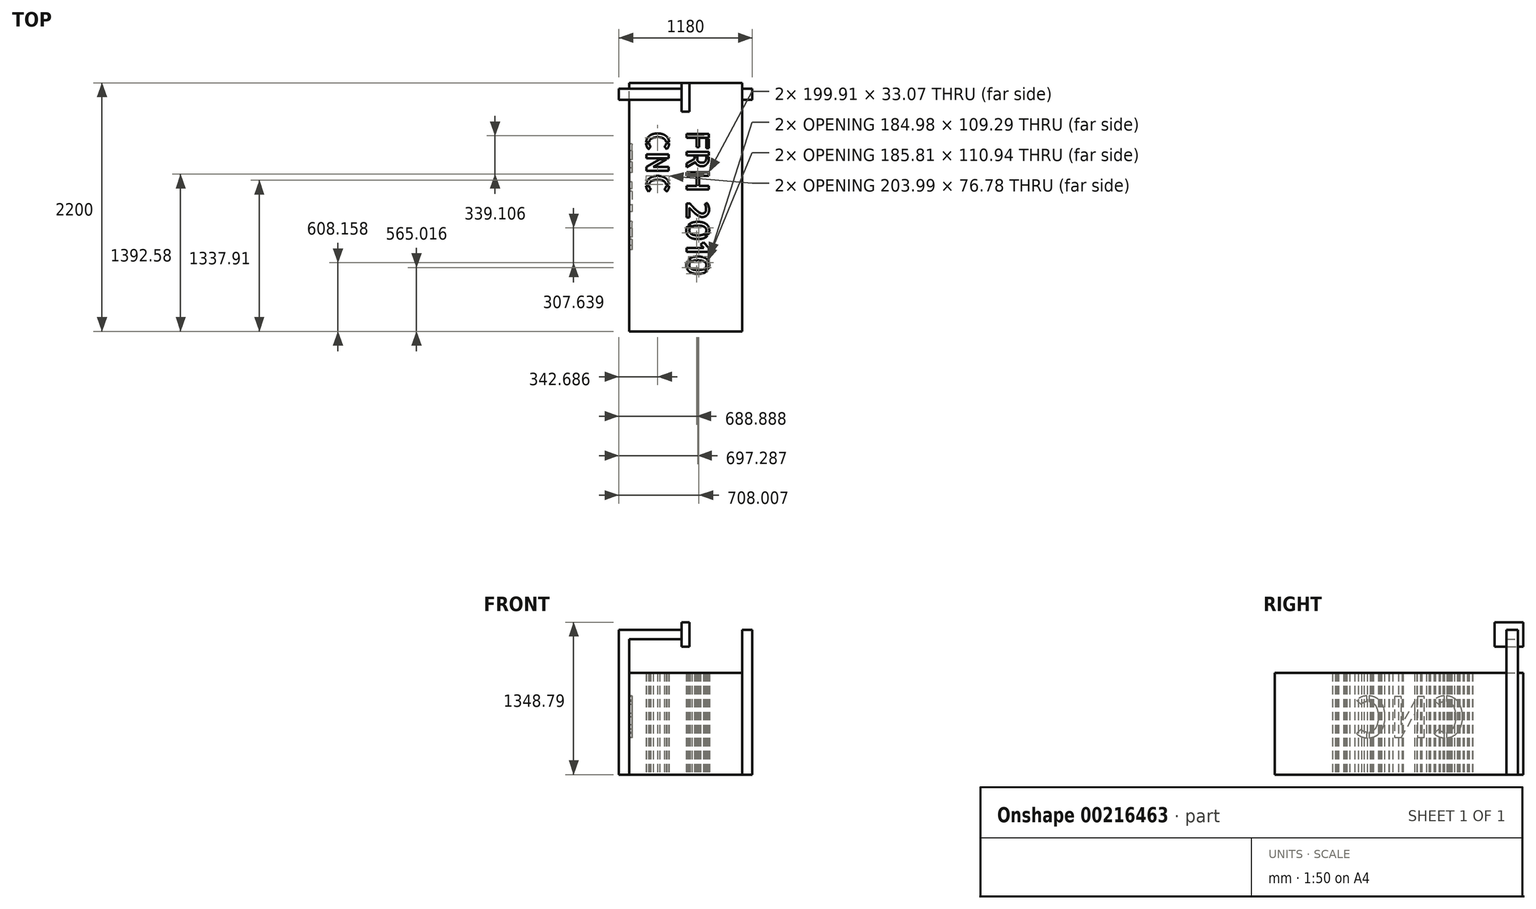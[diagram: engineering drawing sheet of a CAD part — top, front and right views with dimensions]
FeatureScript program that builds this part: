
annotation { "Feature Type Name" : "Feature", "Feature Type Description" : "" }
export const myFeature = defineFeature(function(context is Context, id is Id, definition is map)
    precondition{}
    {
        {
            var Q0;
            Q0=qCreatedBy(makeId("Top.planeOp"),FACE);
            var sketch = newSketch(context, id + "F0", { "sketchPlane" : qUnion([Q0])});
            skLineSegment(sketch, "E0.bottom", {"start": v(1025.88, 14.14) * mm, "end": v(25.88, 14.14) * mm});
            skLineSegment(sketch, "E0.top", {"start": v(1025.88, 2214.14) * mm, "end": v(25.88, 2214.14) * mm});
            skLineSegment(sketch, "E0.left", {"start": v(1025.88, 14.14) * mm, "end": v(1025.88, 2214.14) * mm});
            skLineSegment(sketch, "E0.right", {"start": v(25.88, 14.14) * mm, "end": v(25.88, 2214.14) * mm});
            skText(sketch, "E1", { "text": "FRH 2010\nCNC", "fontName": "AllertaStencil-Regular.ttf"});
            const initialGuessF0  = {"E1": [0.53321, 1.78814, 0, -1, 0.2]};
            skSetInitialGuess(sketch, initialGuessF0);
            skSolve(sketch);
        }
        {
            var Q0;
            Q0=makeQuery(id+"F0.imprint","IMPRINT",FACE,{"disambiguationData":[TD([[makeQuery(id+"F0.imprint","IMPRINT",EDGE,{"derivedFrom":sQuery(id+"F0.wireOp",EDGE,"E0.bottom")}),-1.0]])]});
            extrude(context, id + "F1", {"entities" : qUnion([Q0]), "depth" : 900 * mm});
        }
        {
            var Q0;
            Q0=makeQuery(id+"F1.opExtrude","SWEPT_FACE",FACE,{"disambiguationData":[OSD([sQuery(id+"F0.wireOp",EDGE,"E0.top")])]});
            var sketch = newSketch(context, id + "F2", { "sketchPlane" : qUnion([Q0])});
            skLineSegment(sketch, "E2.bottom", {"start": v(-1025.88, 0) * mm, "end": v(-1115.88, 0) * mm});
            skLineSegment(sketch, "E2.top", {"start": v(-1025.88, 1280) * mm, "end": v(-1115.88, 1280) * mm});
            skLineSegment(sketch, "E2.left", {"start": v(-1025.88, 0) * mm, "end": v(-1025.88, 1280) * mm});
            skLineSegment(sketch, "E2.right", {"start": v(-1115.88, 0) * mm, "end": v(-1115.88, 1280) * mm});
            skLineSegment(sketch, "E3.bottom", {"start": v(-1025.88, 1280) * mm, "end": v(-25.88, 1280) * mm});
            skLineSegment(sketch, "E3.top", {"start": v(-1025.88, 1200) * mm, "end": v(-25.88, 1200) * mm});
            skLineSegment(sketch, "E3.left", {"start": v(-1025.88, 1280) * mm, "end": v(-1025.88, 1200) * mm});
            skLineSegment(sketch, "E3.right", {"start": v(-25.88, 1280) * mm, "end": v(-25.88, 1200) * mm});
            skLineSegment(sketch, "E4", {"start": v(-525.88, -229.17) * mm, "end": v(-525.88, -541.3) * mm, "construction": true});
            skPoint(sketch, "E4.startSnap0", {"position": v(-525.88, 0) * mm});
            skLineSegment(sketch, "E5.MirrorCS", {"start": v(-25.88, 0) * mm, "end": v(-25.88, 1280) * mm});
            skLineSegment(sketch, "E6.MirrorCS", {"start": v(64.12, 0) * mm, "end": v(64.12, 1280) * mm});
            skLineSegment(sketch, "E7.MirrorCS", {"start": v(-25.88, 0) * mm, "end": v(64.12, 0) * mm});
            skLineSegment(sketch, "E8.MirrorCS", {"start": v(-25.88, 1280) * mm, "end": v(64.12, 1280) * mm});
            skPoint(sketch, "E9", {"position": v(-525.88, 1200) * mm});
            skLineSegment(sketch, "E10.bottom", {"start": v(-490.88, 1348.8) * mm, "end": v(-560.88, 1348.8) * mm});
            skLineSegment(sketch, "E10.top", {"start": v(-490.88, 1131.2) * mm, "end": v(-560.88, 1131.2) * mm});
            skLineSegment(sketch, "E10.left", {"start": v(-490.88, 1348.8) * mm, "end": v(-490.88, 1131.2) * mm});
            skLineSegment(sketch, "E10.right", {"start": v(-560.88, 1348.8) * mm, "end": v(-560.88, 1131.2) * mm});
            skPoint(sketch, "E10.middle", {"position": v(-525.88, 1240) * mm});
            skPoint(sketch, "E10.middle.positionSnap0", {"position": v(-1025.88, 1240) * mm});
            skPoint(sketch, "E10.centerSnap0", {"position": v(-1025.88, 1240) * mm});
            skSolve(sketch);
        }
        {
            var Q0;
            {var subQ0=sQuery(id+"F2.wireOp",EDGE,"E5.MirrorCS");var subQ5=sQuery(id+"F2.wireOp",EDGE,"E3.top");var subQ6=makeQuery(id+"F2.imprint","INTERSECT",VERTEX,{"derivedFrom":[subQ5,subQ0]});Q0=makeQuery(id+"F2.imprint","IMPRINT",FACE,{"disambiguationData":[TD([[makeQuery(id+"F2.imprint","IMPRINT",EDGE,{"disambiguationData":[TD([[subQ6,1.0]])],"derivedFrom":subQ5}),1.0]])]});}
            var Q1;
            {var subQ0=sQuery(id+"F2.wireOp",EDGE,"E3.left");Q1=makeQuery(id+"F2.imprint","IMPRINT",FACE,{"disambiguationData":[TD([[makeQuery(id+"F2.imprint","IMPRINT",EDGE,{"derivedFrom":subQ0}),1.0]])]});}
            var Q2;
            {var subQ4=sQuery(id+"F2.wireOp",EDGE,"E2.bottom");Q2=makeQuery(id+"F2.imprint","IMPRINT",FACE,{"disambiguationData":[TD([[makeQuery(id+"F2.imprint","IMPRINT",EDGE,{"derivedFrom":subQ4}),-1.0]])]});}
            var Q3;
            Q3=makeQuery(id+"F2.imprint","IMPRINT",FACE,{"disambiguationData":[TD([[makeQuery(id+"F2.imprint","IMPRINT",EDGE,{"derivedFrom":sQuery(id+"F2.wireOp",EDGE,"E6.MirrorCS")}),1.0]])]});
            extrude(context, id + "F3", {"entities" : qUnion([Q0, Q1, Q2, Q3]), "operationType" : NewBodyOperationType.ADD, "oppositeDirection" : true, "depth" : 150 * mm, "hasSecondDirection" : true, "secondDirectionOppositeDirection" : true, "secondDirectionDepth" : 50 * mm});
        }
        {
            var Q0;
            {var subQ5=sQuery(id+"F2.wireOp",EDGE,"E10.bottom");Q0=makeQuery(id+"F2.imprint","IMPRINT",FACE,{"disambiguationData":[TD([[makeQuery(id+"F2.imprint","IMPRINT",EDGE,{"derivedFrom":subQ5}),1.0]])]});}
            var Q1;
            {var subQ0=sQuery(id+"F2.wireOp",EDGE,"E10.right");var subQ1=sQuery(id+"F2.wireOp",EDGE,"E3.bottom");var subQ2=makeQuery(id+"F2.imprint","INTERSECT",VERTEX,{"derivedFrom":[subQ1,subQ0]});Q1=makeQuery(id+"F2.imprint","IMPRINT",FACE,{"disambiguationData":[TD([[makeQuery(id+"F2.imprint","IMPRINT",EDGE,{"disambiguationData":[TD([[subQ2,-1.0]])],"derivedFrom":subQ1}),-1.0]])]});}
            var Q2;
            {var subQ5=sQuery(id+"F2.wireOp",EDGE,"E10.top");Q2=makeQuery(id+"F2.imprint","IMPRINT",FACE,{"disambiguationData":[TD([[makeQuery(id+"F2.imprint","IMPRINT",EDGE,{"derivedFrom":subQ5}),-1.0]])]});}
            extrude(context, id + "F4", {"entities" : qUnion([Q0, Q1, Q2]), "operationType" : NewBodyOperationType.ADD, "oppositeDirection" : true, "depth" : 255 * mm});
        }
        {
            var Q0;
            {var subQ229=sQuery(id+"F0.wireOp",EDGE,"E0.right");var subQ232=sQuery(id+"F0.wireOp",EDGE,"E0.bottom");Q0=makeQuery(id+"F3.boolean.opBoolean","SPLIT",FACE,{"disambiguationData":[TD([makeQuery(id+"F1.opExtrude","SWEPT_FACE",FACE,{"disambiguationData":[OSD([subQ232])]})])],"derivedFrom":makeQuery(id+"F1.opExtrude","SWEPT_FACE",FACE,{"disambiguationData":[OSD([subQ229])]})});}
            var sketch = newSketch(context, id + "F5", { "sketchPlane" : qUnion([Q0])});
            skText(sketch, "E11", { "text": "CNC", "fontName": "AllertaStencil-Regular.ttf"});
            const initialGuessF5  = {"E11": [-1.71342, 0.32769, 1, 0, 0.36437]};
            skSetInitialGuess(sketch, initialGuessF5);
            skSolve(sketch);
        }
        {
            var Q0;
            Q0=makeQuery(id+"F5.imprint","IMPRINT",FACE,{"disambiguationData":[TD([[makeQuery(id+"F5.imprint","IMPRINT",EDGE,{"derivedFrom":sQuery(id+"F5.wireOp",EDGE,"E11.sketch_text.stroke-5")}),-1.0]])]});
            var Q1;
            Q1=makeQuery(id+"F5.imprint","IMPRINT",FACE,{"disambiguationData":[TD([[makeQuery(id+"F5.imprint","IMPRINT",EDGE,{"derivedFrom":sQuery(id+"F5.wireOp",EDGE,"E11.sketch_text.stroke-0")}),-1.0]])]});
            var Q2;
            Q2=makeQuery(id+"F5.imprint","IMPRINT",FACE,{"disambiguationData":[TD([[makeQuery(id+"F5.imprint","IMPRINT",EDGE,{"derivedFrom":sQuery(id+"F5.wireOp",EDGE,"E11.sketch_text.stroke-36")}),-1.0]])]});
            var Q3;
            Q3=makeQuery(id+"F5.imprint","IMPRINT",FACE,{"disambiguationData":[TD([[makeQuery(id+"F5.imprint","IMPRINT",EDGE,{"derivedFrom":sQuery(id+"F5.wireOp",EDGE,"E11.sketch_text.stroke-29")}),-1.0]])]});
            var Q4;
            Q4=makeQuery(id+"F5.imprint","IMPRINT",FACE,{"disambiguationData":[TD([[makeQuery(id+"F5.imprint","IMPRINT",EDGE,{"derivedFrom":sQuery(id+"F5.wireOp",EDGE,"E11.sketch_text.stroke-51")}),-1.0]])]});
            var Q5;
            Q5=makeQuery(id+"F5.imprint","IMPRINT",FACE,{"disambiguationData":[TD([[makeQuery(id+"F5.imprint","IMPRINT",EDGE,{"derivedFrom":sQuery(id+"F5.wireOp",EDGE,"E11.sketch_text.stroke-40")}),-1.0]])]});
            var Q6;
            Q6=makeQuery(id+"F5.imprint","IMPRINT",FACE,{"disambiguationData":[TD([[makeQuery(id+"F5.imprint","IMPRINT",EDGE,{"derivedFrom":sQuery(id+"F5.wireOp",EDGE,"E11.sketch_text.stroke-45")}),-1.0]])]});
            var Q7;
            Q7=makeQuery(id+"F5.imprint","IMPRINT",FACE,{"disambiguationData":[TD([[makeQuery(id+"F5.imprint","IMPRINT",EDGE,{"derivedFrom":sQuery(id+"F5.wireOp",EDGE,"E11.sketch_text.stroke-11")}),-1.0]])]});
            extrude(context, id + "F6", {"entities" : qUnion([Q0, Q1, Q2, Q3, Q4, Q5, Q6, Q7]), "operationType" : NewBodyOperationType.REMOVE, "oppositeDirection" : true, "depth" : 25 * mm});
        }
    });
